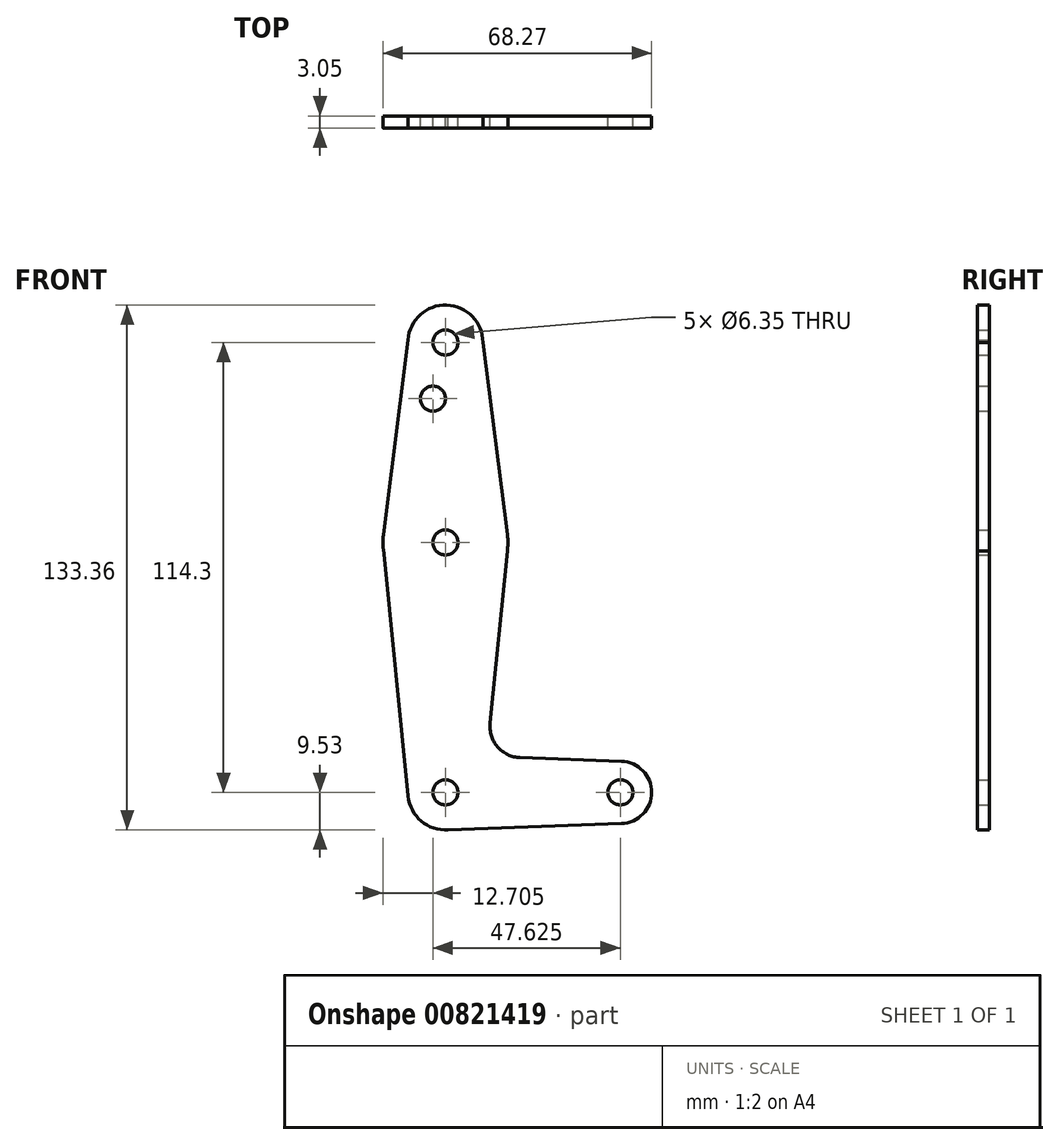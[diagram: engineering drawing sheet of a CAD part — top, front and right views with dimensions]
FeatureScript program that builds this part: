
annotation { "Feature Type Name" : "Feature", "Feature Type Description" : "" }
export const myFeature = defineFeature(function(context is Context, id is Id, definition is map)
    precondition{}
    {
        {
            var Q0;
            Q0=qCreatedBy(makeId("Front.planeOp"),FACE);
            var sketch = newSketch(context, id + "F0", { "sketchPlane" : qUnion([Q0])});
            skLineSegment(sketch, "E0", {"start": v(0, 114.3) * mm, "end": v(0, 0) * mm, "construction": true});
            skLineSegment(sketch, "E1", {"start": v(0, 0) * mm, "end": v(44.45, 0) * mm, "construction": true});
            skCircle(sketch, "E2", {"center": v(0, 0) * mm, "radius": 9.53 * mm});
            skCircle(sketch, "E3", {"center": v(0, 114.3) * mm, "radius": 9.53 * mm});
            skCircle(sketch, "E4", {"center": v(0, 63.5) * mm, "radius": 15.88 * mm});
            skCircle(sketch, "E5", {"center": v(44.45, 0) * mm, "radius": 7.94 * mm});
            skLineSegment(sketch, "E6", {"start": v(-9.5, 114.95) * mm, "end": v(-15.75, 65.49) * mm});
            skLineSegment(sketch, "E7", {"start": v(9.52, 114.3) * mm, "end": v(15.75, 65.5) * mm});
            skLineSegment(sketch, "E8", {"start": v(15.73, 61.35) * mm, "end": v(11.34, 17.59) * mm});
            skLineSegment(sketch, "E9", {"start": v(-15.8, 62.03) * mm, "end": v(-9.48, -0.95) * mm});
            skLineSegment(sketch, "E10", {"start": v(18.97, 8.85) * mm, "end": v(44.73, 7.93) * mm});
            skLineSegment(sketch, "E11", {"start": v(0, -9.53) * mm, "end": v(44.73, -7.93) * mm});
            skCircle(sketch, "E12", {"center": v(0, 114.3) * mm, "radius": 3.18 * mm});
            skCircle(sketch, "E13", {"center": v(-3.17, 100.03) * mm, "radius": 3.18 * mm});
            skCircle(sketch, "E14", {"center": v(0, 63.5) * mm, "radius": 3.17 * mm});
            skCircle(sketch, "E15", {"center": v(0, 0) * mm, "radius": 3.18 * mm});
            skCircle(sketch, "E16", {"center": v(44.45, 0) * mm, "radius": 3.18 * mm});
            skArc(sketch, "E17.filletArc", {"start": v(11.34, 17.59) * mm, "mid": v(13.26, 11.57) * mm, "end": v(18.97, 8.85) * mm});
            skSolve(sketch);
        }
        {
            var Q0;
            Q0 = qSketchRegion(id + "F0", true);
            extrude(context, id + "F1", {"entities" : qUnion([Q0]), "depth" : 3.05 * mm, "offsetDistance" : 25.4 * mm});
        }
    });
